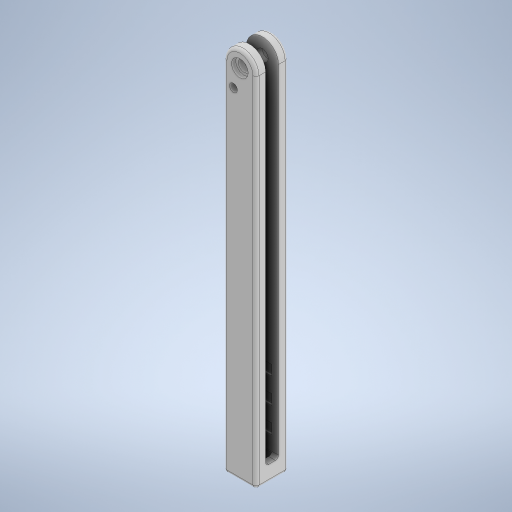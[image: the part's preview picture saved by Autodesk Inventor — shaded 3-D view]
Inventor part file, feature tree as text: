
AUTODESK INVENTOR PART (.ipt)
format: ipt  version: 2023.5 (Build 275446000, 446)  size: 361,472 bytes
history: native  units: mm
features: extrude x6, sketch x5, fillet x1, plane x1, mirror x1, projected_geometry x1
ambient origin geometry x8: Origin, YZ Plane, XZ Plane, XY Plane, X Axis, Y Axis, Z Axis, Center Point
bodies: Solid1 (feature_tree)
feature tree (15):
  extrude  "Extrusion1"  Depth=12.7mm
  sketch  "Sketch2"  dims[d2=4.572mm d3=12.7mm d4=0.0mm]
  extrude  "Extrusion2"  Depth=12.7mm TaperAngle=0.0deg
  extrude  "Extrusion3"  Depth=5.08mm
  extrude  "Extrusion4"  Depth=120.048mm
  fillet  "Fillet1"  Radius=5.08mm
  extrude  "Extrusion6"  Depth=8.89mm TaperAngle=0.0deg
  plane  "Work Plane1"
  mirror  "Mirror1"
  extrude  "Extrusion7"  TaperAngle=0.0deg  [1 undecoded]
  sketch  "Sketch1"  dims[d0=12.7mm d1=140.97mm]
  sketch  "Sketch3"  dims[d5=6.35mm d6=5.08mm]
  sketch  "Sketch5"  dims[d7=3.81mm d8=120.048mm d9=5.08mm]
  sketch  "Sketch6"  dims[d10=24.0mm d11=8.89mm d12=0.0mm d13=0.0mm d14=0.0mm d15=3.175mm d16=7.954mm d17=2.54mm d18=0.0mm d19=0.0mm d20=1.2mm d25=6.604mm d26=1.651mm d27=0.0mm d28=1.5mm d29=2.0mm d30=7.0mm d31=4.0mm d32=10.0mm d34=10.0mm d35=40.0mm d37=10.0mm d39=10.0mm d40=0.0mm]
  projected_geometry  "Projected Loop1"
note: 1 required parameter value undecoded (feature->parameter linkage not recoverable at this tier; creation-order binding heuristic only, values carry confidence <= 0.55)
